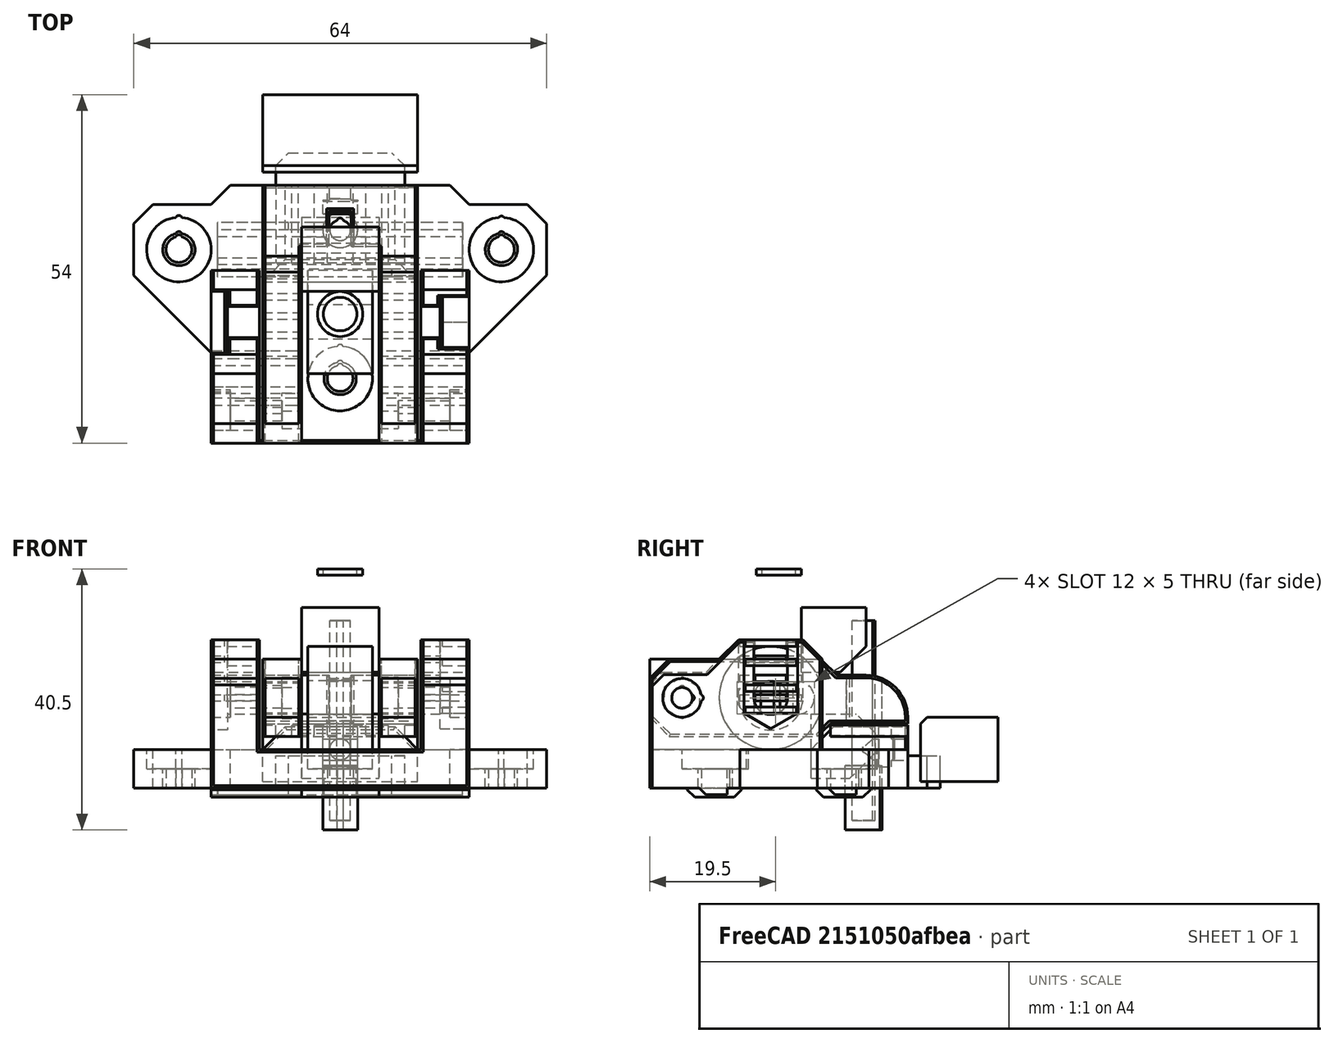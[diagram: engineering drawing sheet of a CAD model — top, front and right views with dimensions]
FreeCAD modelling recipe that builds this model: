
FCSTD DOCUMENT  (FreeCAD 0.18R14555 (Git shallow))
Label: y-idler-10mm-lower-rev
License: All rights reserved
LicenseURL: http://en.wikipedia.org/wiki/All_rights_reserved
objects: Part::Box×72, Part::Cylinder×41, Part::MultiFuse×41, Part::Cut×37, Part::Chamfer×27, Part::Feature×24, Part::Fillet×1
note: 243 computed .brp shape members not serialized (recipe doc carries the construction recipe); baked Part::Feature solids carry a one-line shape summary decoded from their .brp

FEATURE [Part::Box] Box  label="Cube"
  AttacherType = Attacher::AttachEngine3D
  Height = 10
  Length = 40
  Placement = pos=(-20,-20,-10) rot=(0,0,1;0rad)
  Width = 40
FEATURE [Part::Box] Box001  label="Cube001"
  AttacherType = Attacher::AttachEngine3D
  Height = 12
  Length = 6
  Placement = pos=(6,-20,4) rot=(0,0,1;0rad)
  Width = 43
FEATURE [Part::Box] Box002  label="Cube002"
  AttacherType = Attacher::AttachEngine3D
  Height = 12
  Length = 6
  Placement = pos=(-12,-20,4) rot=(0,0,1;0rad)
  Width = 43
FEATURE [Part::Box] Box003  label="Cube003"
  AttacherType = Attacher::AttachEngine3D
  Height = 12
  Length = 12
  Placement = pos=(-6,10.5,3) rot=(0,0,1;0rad)
  Width = 12.5
FEATURE [Part::Cylinder] Cylinder  label="idler"
  Angle = 360
  AttacherType = Attacher::AttachEngine3D
  Height = 10
  Placement = pos=(5,-1.25,10) rot=(0,-1,0;1.5708rad)
  Radius = 8
FEATURE [Part::Cylinder] Cylinder001
  Angle = 360
  AttacherType = Attacher::AttachEngine3D
  Height = 6
  Placement = pos=(6,-2,15) rot=(0,1,0;1.5708rad)
  Radius = 2.5
FEATURE [Part::Cylinder] Cylinder002
  Angle = 360
  AttacherType = Attacher::AttachEngine3D
  Height = 6
  Placement = pos=(-12,5,15) rot=(0,1,0;1.5708rad)
  Radius = 2.5
FEATURE [Part::Cylinder] Cylinder003
  Angle = 360
  AttacherType = Attacher::AttachEngine3D
  Height = 6
  Placement = pos=(-12,-2,15) rot=(0,1,0;1.5708rad)
  Radius = 2.5
FEATURE [Part::Cylinder] Cylinder004
  Angle = 360
  AttacherType = Attacher::AttachEngine3D
  Height = 6
  Placement = pos=(6,5,15) rot=(0,1,0;1.5708rad)
  Radius = 2.5
FEATURE [Part::Box] Box005  label="Cube005"
  AttacherType = Attacher::AttachEngine3D
  Height = 5
  Length = 6
  Placement = pos=(6,-2,12.5) rot=(0,0,1;0rad)
  Width = 7
FEATURE [Part::Box] Box006  label="Cube006"
  AttacherType = Attacher::AttachEngine3D
  Height = 5
  Length = 6
  Placement = pos=(-12,-2,12.5) rot=(0,0,1;0rad)
  Width = 7
FEATURE [Part::MultiFuse] Fusion
  Placement = pos=(0,-2,-5) rot=(0,0,1;0rad)
  Shapes = -> [Box005,Cylinder001,Cylinder004]
FEATURE [Part::MultiFuse] Fusion001
  Placement = pos=(0,-2,-5) rot=(0,0,1;0rad)
  Shapes = -> [Box006,Cylinder003,Cylinder002]
FEATURE [Part::Box] Box007  label="Cube007"
  AttacherType = Attacher::AttachEngine3D
  Height = 14
  Length = 7.5
  Placement = pos=(-20,-20,1) rot=(0,0,1;0rad)
  Width = 11
FEATURE [Part::Box] Box008  label="Cube008"
  AttacherType = Attacher::AttachEngine3D
  Height = 14
  Length = 7.5
  Placement = pos=(12.5,-20,1) rot=(0,0,1;0rad)
  Width = 11
FEATURE [Part::Box] Box009  label="Cube009"
  AttacherType = Attacher::AttachEngine3D
  Height = 20
  Length = 7.5
  Placement = pos=(-20,-10,0) rot=(0,0,1;0rad)
  Width = 18
FEATURE [Part::Box] Box010  label="Cube010"
  AttacherType = Attacher::AttachEngine3D
  Height = 20
  Length = 7.5
  Placement = pos=(12.5,-10,0) rot=(0,0,1;0rad)
  Width = 18
FEATURE [Part::Chamfer] Chamfer
  Base = -> Box009
  Edges = 2 edges r=4: [Edge10,Edge12]
FEATURE [Part::Chamfer] Chamfer001
  Base = -> Box010
  Edges = 2 edges r=4: [Edge10,Edge12]
FEATURE [Part::Cylinder] Cylinder005  label="Cylinder"
  Angle = 360
  AttacherType = Attacher::AttachEngine3D
  Height = 8
  Placement = pos=(-12,0,10) rot=(0,-1,0;1.5708rad)
  Radius = 2.6
FEATURE [Part::Cylinder] Cylinder006  label="Cylinder005"
  Angle = 360
  AttacherType = Attacher::AttachEngine3D
  Height = 8
  Placement = pos=(20,0,10) rot=(0,-1,0;1.5708rad)
  Radius = 2.6
FEATURE [Part::Box] Box011  label="Cube011"
  AttacherType = Attacher::AttachEngine3D
  Height = 10
  Length = 8
  Placement = pos=(12,-2.6,10) rot=(0,0,1;0rad)
  Width = 5.2
FEATURE [Part::Box] Box012  label="Cube012"
  AttacherType = Attacher::AttachEngine3D
  Height = 10
  Length = 8
  Placement = pos=(-20,-2.6,10) rot=(0,0,1;0rad)
  Width = 5.2
FEATURE [Part::Cylinder] Cylinder007  label="Cylinder006"
  Angle = 360
  AttacherType = Attacher::AttachEngine3D
  Height = 31
  Placement = pos=(0,16,-10) rot=(0,0,1;0rad)
  Radius = 1.6
FEATURE [Part::Cylinder] Cylinder008  label="Cylinder007"
  Angle = 360
  AttacherType = Attacher::AttachEngine3D
  Height = 3
  Placement = pos=(25,10,-3) rot=(0,0,1;0rad)
  Radius = 5
FEATURE [Part::Cylinder] Cylinder009  label="Cylinder008"
  Angle = 360
  AttacherType = Attacher::AttachEngine3D
  Height = 8
  Placement = pos=(-12,-15,10) rot=(0,-1,0;1.5708rad)
  Radius = 1.6
FEATURE [Part::Cylinder] Cylinder010  label="Cylinder009"
  Angle = 360
  AttacherType = Attacher::AttachEngine3D
  Height = 8
  Placement = pos=(20,-15,10) rot=(0,-1,0;1.5708rad)
  Radius = 1.6
FEATURE [Part::Cylinder] Cylinder011  label="Cylinder010"
  Angle = 360
  AttacherType = Attacher::AttachEngine3D
  Height = 24
  Placement = pos=(12,-15,10) rot=(0,-1,0;1.5708rad)
  Radius = 1.6
FEATURE [Part::Cylinder] Cylinder012  label="Cylinder011"
  Angle = 360
  AttacherType = Attacher::AttachEngine3D
  Height = 3
  Placement = pos=(-25,10,-3) rot=(0,0,1;0rad)
  Radius = 5
FEATURE [Part::Box] Box014  label="Cube014"
  AttacherType = Attacher::AttachEngine3D
  Height = 10
  Length = 64
  Placement = pos=(-32,-6,-10) rot=(0,0,1;0rad)
  Width = 23
FEATURE [Part::Chamfer] Chamfer004
  Base = -> Box014
  Edges = 2 edges r=12: [Edge1,Edge5]
FEATURE [Part::Chamfer] Chamfer005
  Base = -> Box
  Edges = 2 edges r=3: [Edge3,Edge7]
FEATURE [Part::Chamfer] Chamfer006
  Base = -> Chamfer004
  Edges = 2 edges r=3: [Edge3,Edge13]
FEATURE [Part::Cylinder] Cylinder013  label="Cylinder012"
  Angle = 360
  AttacherType = Attacher::AttachEngine3D
  Height = 24
  Placement = pos=(12,-15,11.4) rot=(0,-1,0;1.5708rad)
  Radius = 0.5
FEATURE [Part::Cylinder] Cylinder014  label="Cylinder013"
  Angle = 360
  AttacherType = Attacher::AttachEngine3D
  Height = 8
  Placement = pos=(20,-13.6,10) rot=(0,-1,0;1.5708rad)
  Radius = 0.5
FEATURE [Part::Cylinder] Cylinder015  label="Cylinder014"
  Angle = 360
  AttacherType = Attacher::AttachEngine3D
  Height = 8
  Placement = pos=(-12,-13.6,10) rot=(0,-1,0;1.5708rad)
  Radius = 0.5
FEATURE [Part::Cylinder] Cylinder016  label="Cylinder015"
  Angle = 360
  AttacherType = Attacher::AttachEngine3D
  Height = 15
  Placement = pos=(-25,10,-10) rot=(0,0,1;0rad)
  Radius = 2.5
FEATURE [Part::Cylinder] Cylinder017  label="Cylinder016"
  Angle = 360
  AttacherType = Attacher::AttachEngine3D
  Height = 15
  Placement = pos=(25,10,-10) rot=(0,0,1;0rad)
  Radius = 2.5
FEATURE [Part::Cylinder] Cylinder018  label="Cylinder019"
  Angle = 360
  AttacherType = Attacher::AttachEngine3D
  Height = 15
  Placement = pos=(25,12.3,-10) rot=(0,0,1;0rad)
  Radius = 0.5
FEATURE [Part::Cylinder] Cylinder019  label="Cylinder020"
  Angle = 360
  AttacherType = Attacher::AttachEngine3D
  Height = 15
  Placement = pos=(-25,12.3,-10) rot=(0,0,1;0rad)
  Radius = 0.5
FEATURE [Part::Cylinder] Cylinder020  label="Cylinder021"
  Angle = 360
  AttacherType = Attacher::AttachEngine3D
  Height = 31
  Placement = pos=(0,17.4,-10) rot=(0,0,1;0rad)
  Radius = 0.5
FEATURE [Part::Cylinder] Cylinder021  label="Cylinder022"
  Angle = 360
  AttacherType = Attacher::AttachEngine3D
  Height = 15
  Placement = pos=(0,-10,-10) rot=(0,0,1;0rad)
  Radius = 2.5
FEATURE [Part::Cylinder] Cylinder023  label="Cylinder024"
  Angle = 360
  AttacherType = Attacher::AttachEngine3D
  Height = 15
  Placement = pos=(0,-7.7,-10) rot=(0,0,1;0rad)
  Radius = 0.5
FEATURE [Part::Cylinder] Cylinder024  label="Cylinder025"
  Angle = 360
  AttacherType = Attacher::AttachEngine3D
  Height = 2.5
  Placement = pos=(-17.5,0,10) rot=(0,-1,0;1.5708rad)
  Radius = 5
FEATURE [Part::Box] Box015  label="Cube015"
  AttacherType = Attacher::AttachEngine3D
  Height = 10
  Length = 2.5
  Placement = pos=(-20,-5,10) rot=(0,0,1;0rad)
  Width = 10
FEATURE [Part::Feature] Fusion010001  label="Fusion011"
  Placement = pos=(0,5.775,5) rot=(0,0,1;0rad)
  shape: bbox 40 x 8.45 x 1.4 mm, 38 faces (baked)
FEATURE [Part::Feature] Fusion010002  label="Fusion012"
  Placement = pos=(12,25.77,5) rot=(0,0,1;0rad)
  shape: bbox 40 x 8.45 x 1.4 mm, 38 faces (baked)
FEATURE [Part::Feature] Fusion010003  label="Fusion013"
  Placement = pos=(-12,25.765,5) rot=(0,0,1;0rad)
  shape: bbox 40 x 8.45 x 1.4 mm, 38 faces (baked)
FEATURE [Part::Cylinder] Cylinder025  label="Cylinder026"
  Angle = 360
  AttacherType = Attacher::AttachEngine3D
  Height = 3
  Placement = pos=(0,-10,-3) rot=(0,0,1;0rad)
  Radius = 5
FEATURE [Part::Cylinder] Cylinder026  label="Cylinder027"
  Angle = 360
  AttacherType = Attacher::AttachEngine3D
  Height = 3
  Placement = pos=(0,-5.2,-3) rot=(0,0,1;0rad)
  Radius = 0.5
FEATURE [Part::Cylinder] Cylinder027  label="Cylinder028"
  Angle = 360
  AttacherType = Attacher::AttachEngine3D
  Height = 3
  Placement = pos=(-25,14.8,-3) rot=(0,0,1;0rad)
  Radius = 0.5
FEATURE [Part::Cylinder] Cylinder028  label="Cylinder029"
  Angle = 360
  AttacherType = Attacher::AttachEngine3D
  Height = 3
  Placement = pos=(25,14.7,-3) rot=(0,0,1;0rad)
  Radius = 0.5
FEATURE [Part::MultiFuse] Fusion010005
  Shapes = -> [Cylinder025,Cylinder012,Cylinder008]
FEATURE [Part::Box] Box017  label="Cube017"
  AttacherType = Attacher::AttachEngine3D
  Height = 10
  Length = 10
  Placement = pos=(-60,0,-20) rot=(0,0,1;0rad)
  Width = 10
FEATURE [Part::Box] Box018  label="Cube018"
  AttacherType = Attacher::AttachEngine3D
  Height = 10
  Length = 10
  Placement = pos=(-40,0,-20) rot=(0,0,1;0rad)
  Width = 10
FEATURE [Part::Box] Box019  label="Cube019"
  AttacherType = Attacher::AttachEngine3D
  Height = 10
  Length = 10
  Placement = pos=(40,0,-20) rot=(0,0,1;0rad)
  Width = 10
FEATURE [Part::Box] Box020  label="Cube020"
  AttacherType = Attacher::AttachEngine3D
  Height = 10
  Length = 10
  Placement = pos=(40,0,-20) rot=(0,0,1;0rad)
  Width = 10
FEATURE [Part::Chamfer] Chamfer016
  Base = -> Box018
  Edges = 1 edges r=4: [Edge5]
  Placement = pos=(0,12,5) rot=(0,0,1;0rad)
FEATURE [Part::Chamfer] Chamfer017
  Base = -> Box017
  Edges = 1 edges r=4: [Edge7]
  Placement = pos=(20,-2,5) rot=(0,0,1;0rad)
FEATURE [Part::Chamfer] Chamfer018
  Base = -> Box019
  Edges = 1 edges r=4: [Edge3]
  Placement = pos=(-11,-3,5) rot=(0,0,1;0rad)
FEATURE [Part::Chamfer] Chamfer019
  Base = -> Box020
  Edges = 1 edges r=4: [Edge1]
  Placement = pos=(-9,11,5) rot=(0,0,1;0rad)
FEATURE [Part::Cylinder] Cylinder030  label="Cylinder031"
  Angle = 360
  AttacherType = Attacher::AttachEngine3D
  Height = 3
  Placement = pos=(-20,-12.2,10) rot=(0,1,0;1.5708rad)
  Radius = 0.5
FEATURE [Part::Cylinder] Cylinder031  label="Cylinder032"
  Angle = 360
  AttacherType = Attacher::AttachEngine3D
  Height = 3
  Placement = pos=(-20,-15,10) rot=(0,1,0;1.5708rad)
  Radius = 3
FEATURE [Part::Feature] Body005001  label="Body006"
  Placement = pos=(-9,-15,10) rot=(1,0,0;1.5708rad)
  shape: bbox 3 x 5.543 x 6.4 mm, 8 faces (baked)
FEATURE [Part::Cylinder] Cylinder032  label="Cylinder033"
  Angle = 360
  AttacherType = Attacher::AttachEngine3D
  Height = 3
  Placement = pos=(17,-15,10) rot=(0,1,0;1.5708rad)
  Radius = 3
FEATURE [Part::Cylinder] Cylinder033  label="Cylinder034"
  Angle = 360
  AttacherType = Attacher::AttachEngine3D
  Height = 3
  Placement = pos=(17,-12.2,10) rot=(0,1,0;1.5708rad)
  Radius = 0.5
FEATURE [Part::MultiFuse] Fusion010006003
  Shapes = -> [Cylinder031,Cylinder030]
FEATURE [Part::MultiFuse] Fusion010006004
  Shapes = -> [Cylinder033,Cylinder032]
FEATURE [Part::Feature] Body005002  label="Body007"
  Placement = pos=(6,-15,10) rot=(1,0,0;1.5708rad)
  shape: bbox 3 x 5.543 x 6.4 mm, 8 faces (baked)
FEATURE [Part::Box] Box029  label="Cube029"
  AttacherType = Attacher::AttachEngine3D
  Height = 1
  Length = 2.1
  Placement = pos=(-20,-3.53,7.5) rot=(0,0,1;0rad)
  Width = 9.6
FEATURE [Part::Box] Box030  label="Cube030"
  AttacherType = Attacher::AttachEngine3D
  Height = 1
  Length = 4.1
  Placement = pos=(15.9,-2.68,5.6) rot=(0,0,1;0rad)
  Width = 7.91
FEATURE [Part::Box] Box032  label="Cube032"
  AttacherType = Attacher::AttachEngine3D
  Height = 1
  Length = 5
  Placement = pos=(-17.5,-1.13,7.5) rot=(0,0,1;0rad)
  Width = 4.8
FEATURE [Part::MultiFuse] Fusion010006008
  Shapes = -> [Box012,Cylinder005]
FEATURE [Part::MultiFuse] Fusion010006009
  Shapes = -> [Cylinder006,Box011]
FEATURE [Part::Cut] Cut022015
  Base = -> Chamfer
  Tool = -> Fusion010006008
FEATURE [Part::Cut] Cut022016
  Base = -> Chamfer001
  Tool = -> Fusion010006009
FEATURE [Part::Feature] Pad002001  label="Pad003"
  Placement = pos=(17.5,0,10) rot=(0.57735,0.57735,0.57735;2.0944rad)
  shape: bbox 10 x 8.314 x 9.6 mm, 8 faces (baked)
FEATURE [Part::Feature] Pad002002  label="Pad004"
  Placement = pos=(17.5,0,14) rot=(0.57735,0.57735,0.57735;2.0944rad)
  shape: bbox 10 x 8.314 x 9.6 mm, 8 faces (baked)
FEATURE [Part::Feature] Pad002003  label="Pad005"
  Placement = pos=(17.5,0,18) rot=(0.57735,0.57735,0.57735;2.0944rad)
  shape: bbox 10 x 8.314 x 9.6 mm, 8 faces (baked)
FEATURE [Part::MultiFuse] Fusion010006010
  Shapes = -> [Pad002003,Pad002001,Pad002002]
FEATURE [Part::Cut] Cut022017  label="base-right-arm-top"
  Base = -> Cut022016
  Placement = pos=(0,1.27,-2) rot=(0,0,1;0rad)
  Tool = -> Fusion010006010
FEATURE [Part::MultiFuse] Fusion010006011
  Shapes = -> [Cylinder024,Box015]
FEATURE [Part::Cut] Cut022018  label="base-left-arm-top"
  Base = -> Cut022015
  Placement = pos=(0,1.27,-2) rot=(0,0,1;0rad)
  Tool = -> Fusion010006011
FEATURE [Part::MultiFuse] Fusion010006014
  Shapes = -> [Cylinder013,Cylinder011]
FEATURE [Part::MultiFuse] Fusion010006015
  Placement = pos=(0,0,-1) rot=(0,0,1;0rad)
  Shapes = -> [Fusion010006014,Body005002,Body005001]
FEATURE [Part::MultiFuse] Fusion010006012003
  Placement = pos=(0,0,-1) rot=(0,0,1;0rad)
  Shapes = -> [Fusion010006003,Cylinder015,Cylinder009]
FEATURE [Part::MultiFuse] Fusion010006012004
  Placement = pos=(0,0,-1) rot=(0,0,1;0rad)
  Shapes = -> [Cylinder010,Cylinder014,Fusion010006004]
FEATURE [Part::MultiFuse] Fusion010006012005
  Placement = pos=(0,0,5) rot=(0,0,1;0rad)
  Shapes = -> [Chamfer006,Chamfer005]
FEATURE [Part::Box] Box038  label="Cube038"
  AttacherType = Attacher::AttachEngine3D
  Height = 5
  Length = 65
  Placement = pos=(-32,-24,1) rot=(0,0,1;0rad)
  Width = 50
FEATURE [Part::MultiFuse] Fusion010006012007
  Shapes = -> [Chamfer018,Chamfer019,Chamfer016,Chamfer017]
FEATURE [Part::MultiFuse] Fusion010006012008
  Placement = pos=(0,0,1) rot=(0,0,1;0rad)
  Shapes = -> [Fusion010005,Cylinder027,Cylinder028,Cylinder026]
FEATURE [Part::Box] Box039  label="Cube039"
  AttacherType = Attacher::AttachEngine3D
  Height = 10
  Length = 40
  Placement = pos=(-26,-25,12) rot=(0,0,1;0rad)
  Width = 20
FEATURE [Part::Chamfer] Chamfer027
  Base = -> Box039
  Edges = 1 edges r=2: [Edge11]
  Placement = pos=(0,-4.25,1) rot=(0,0,1;0rad)
FEATURE [Part::Box] Box040  label="Cube040"
  AttacherType = Attacher::AttachEngine3D
  Height = 10
  Length = 32
  Placement = pos=(-15,24,-8) rot=(0,0,1;0rad)
  Width = 26
FEATURE [Part::Chamfer] Chamfer028
  Base = -> Box040
  Edges = 1 edges r=3: [Edge10]
  Placement = pos=(0,-19,3) rot=(0,0,1;0rad)
FEATURE [Part::Box] Box043  label="cube042"
  AttacherType = Attacher::AttachEngine3D
  Height = 2.8
  Length = 2
  Placement = pos=(-12,11,2) rot=(0,0,1;0rad)
  Width = 12
FEATURE [Part::Box] Box044  label="Cube043"
  AttacherType = Attacher::AttachEngine3D
  Height = 4.6
  Length = 6
  Placement = pos=(-12,-2,5.7) rot=(0,0,1;0rad)
  Width = 1
FEATURE [Part::Box] Box045  label="Cube044"
  AttacherType = Attacher::AttachEngine3D
  Height = 4.6
  Length = 6
  Placement = pos=(6,-2,5.7) rot=(0,0,1;0rad)
  Width = 1
FEATURE [Part::Box] Box052  label="Cube047"
  AttacherType = Attacher::AttachEngine3D
  Height = 4.6
  Length = 6
  Placement = pos=(-12,1,5.7) rot=(0,0,1;0rad)
  Width = 1
FEATURE [Part::Box] Box054  label="Cube049"
  AttacherType = Attacher::AttachEngine3D
  Height = 4.6
  Length = 6
  Placement = pos=(-12,4,5.7) rot=(0,0,1;0rad)
  Width = 1
FEATURE [Part::Box] Box055  label="Cube050"
  AttacherType = Attacher::AttachEngine3D
  Height = 4.6
  Length = 6
  Placement = pos=(6,1,5.7) rot=(0,0,1;0rad)
  Width = 1
FEATURE [Part::Box] Box057  label="Cube052"
  AttacherType = Attacher::AttachEngine3D
  Height = 4.6
  Length = 6
  Placement = pos=(6,4,5.7) rot=(0,0,1;0rad)
  Width = 1
FEATURE [Part::Box] Box058  label="Cube053"
  AttacherType = Attacher::AttachEngine3D
  Height = 1
  Length = 4.1
  Placement = pos=(15.9,-2.68,9) rot=(0,0,1;0rad)
  Width = 7.91
FEATURE [Part::Box] Box059  label="Cube054"
  AttacherType = Attacher::AttachEngine3D
  Height = 1
  Length = 3
  Placement = pos=(12.5,-1.13,7.5) rot=(0,0,1;0rad)
  Width = 4.8
FEATURE [Part::Box] Box063  label="Cube058"
  AttacherType = Attacher::AttachEngine3D
  Height = 1
  Length = 3
  Placement = pos=(12.5,-1.13,10.5) rot=(0,0,1;0rad)
  Width = 4.8
FEATURE [Part::Box] Box064  label="Cube059"
  AttacherType = Attacher::AttachEngine3D
  Height = 1
  Length = 2.1
  Placement = pos=(-20,-3.53,10.5) rot=(0,0,1;0rad)
  Width = 9.6
FEATURE [Part::Box] Box066  label="Cube061"
  AttacherType = Attacher::AttachEngine3D
  Height = 1
  Length = 5
  Placement = pos=(-17.5,-1.13,10.5) rot=(0,0,1;0rad)
  Width = 4.8
FEATURE [Part::Box] Box068  label="Cube063"
  AttacherType = Attacher::AttachEngine3D
  Height = 1
  Length = 3
  Placement = pos=(12.5,-1.13,13.5) rot=(0,0,1;0rad)
  Width = 4.8
FEATURE [Part::Box] Box069  label="Cube064"
  AttacherType = Attacher::AttachEngine3D
  Height = 1
  Length = 2.1
  Placement = pos=(-20,-3.53,13.5) rot=(0,0,1;0rad)
  Width = 9.6
FEATURE [Part::Box] Box070  label="Cube065"
  AttacherType = Attacher::AttachEngine3D
  Height = 1
  Length = 2.1
  Placement = pos=(-20,-3.53,16) rot=(0,0,1;0rad)
  Width = 9.6
FEATURE [Part::Box] Box071  label="Cube066"
  AttacherType = Attacher::AttachEngine3D
  Height = 1
  Length = 5
  Placement = pos=(-17.5,-1.13,16) rot=(0,0,1;0rad)
  Width = 4.8
FEATURE [Part::Box] Box075  label="Cube070"
  AttacherType = Attacher::AttachEngine3D
  Height = 1
  Length = 3
  Placement = pos=(12.5,-1.13,16) rot=(0,0,1;0rad)
  Width = 4.8
FEATURE [Part::Box] Box076  label="Cube071"
  AttacherType = Attacher::AttachEngine3D
  Height = 1
  Length = 5
  Placement = pos=(-17.5,-1.13,13) rot=(0,0,1;0rad)
  Width = 4.8
FEATURE [Part::Box] Box077  label="Cube072"
  AttacherType = Attacher::AttachEngine3D
  Height = 1
  Length = 4.1
  Placement = pos=(15.9,-2.68,16) rot=(0,0,1;0rad)
  Width = 7.91
FEATURE [Part::Box] Box078  label="Cube073"
  AttacherType = Attacher::AttachEngine3D
  Height = 1
  Length = 4.1
  Placement = pos=(15.9,-2.68,13) rot=(0,0,1;0rad)
  Width = 7.91
FEATURE [Part::Box] Box079  label="Cube074"
  AttacherType = Attacher::AttachEngine3D
  Height = 17
  Length = 10
  Placement = pos=(-21,-15,0) rot=(0,0,1;0rad)
  Width = 14
FEATURE [Part::Chamfer] Chamfer030006
  Base = -> Box079
  Edges = 1 edges r=10: [Edge11]
  Placement = pos=(0,2.27,12) rot=(0,0,1;0rad)
FEATURE [Part::Feature] Chamfer030006001  label="Chamfer030007"
  Placement = pos=(32,2.27,12) rot=(0,0,1;0rad)
  shape: bbox 10 x 14 x 17 mm, 7 faces (baked)
FEATURE [Part::Cut] Cut022020016004
  Base = -> Cut022018
  Tool = -> Chamfer030006
FEATURE [Part::Cut] Cut022020016005
  Base = -> Cut022017
  Tool = -> Chamfer030006001
FEATURE [Part::Box] Box080  label="Cube075"
  AttacherType = Attacher::AttachEngine3D
  Height = 10
  Length = 12
  Placement = pos=(-21,-5,17) rot=(0,0,1;0rad)
  Width = 16
FEATURE [Part::Cut] Cut022020016006  label="base-left-arm-top-trim"
  Base = -> Cut022020016004
  Placement = pos=(0,-2.52,1) rot=(0,0,1;0rad)
  Tool = -> Box080
FEATURE [Part::Box] Box081  label="Cube076"
  AttacherType = Attacher::AttachEngine3D
  Height = 10
  Length = 12
  Placement = pos=(9,-5,17) rot=(0,0,1;0rad)
  Width = 16
FEATURE [Part::Cut] Cut022020016007  label="base-right-arm-top-trim"
  Base = -> Cut022020016005
  Placement = pos=(0,2.54,0) rot=(0,0,1;0rad)
  Tool = -> Box081
FEATURE [Part::MultiFuse] Fusion010006012010005014
  Shapes = -> [Box071,Box076,Box066,Box032]
FEATURE [Part::MultiFuse] Fusion010006012010005016
  Shapes = -> [Box029,Box064,Box069,Box070]
FEATURE [Part::Box] Box082  label="Cube077"
  AttacherType = Attacher::AttachEngine3D
  Height = 14
  Length = 2
  Placement = pos=(17.55,-3.1,3) rot=(0,0,1;0rad)
  Width = 9
FEATURE [Part::Feature] Chamfer030006002001  label="arm-rev-4-3-no-support001"
  shape: bbox 64 x 40 x 23.4 mm, 138 faces (baked)
FEATURE [Part::Cut] Cut022020016008
  Base = -> Box082
  Placement = pos=(-2.05,2.54,0) rot=(0,0,1;0rad)
  Tool = -> Chamfer030006002001
FEATURE [Part::MultiFuse] Fusion010006012010005012002
  Shapes = -> [Box059,Box075,Box063,Box068]
FEATURE [Part::MultiFuse] Fusion010006012010005012003
  Shapes = -> [Box030,Box078,Box058,Box077]
FEATURE [Part::MultiFuse] Fusion010006012010005012004  label="base-custom-support"
  Placement = pos=(0,-2.52,1) rot=(0,0,1;0rad)
  Shapes = -> [Fusion010006012010005016,Fusion010006012010005012002,Fusion010006012010005012003,Fusion010006012010005014]
FEATURE [Part::Box] Box083  label="Cube078"
  AttacherType = Attacher::AttachEngine3D
  Height = 10
  Length = 12
  Placement = pos=(-6,-15,-15) rot=(0,0,1;0rad)
  Width = 10
FEATURE [Part::Box] Box084  label="Cube079"
  AttacherType = Attacher::AttachEngine3D
  Height = 10
  Length = 13
  Placement = pos=(19,5,-15) rot=(0,0,1;0rad)
  Width = 10
FEATURE [Part::Box] Box085  label="Cube080"
  AttacherType = Attacher::AttachEngine3D
  Height = 10
  Length = 13
  Placement = pos=(-32,5,-15) rot=(0,0,1;0rad)
  Width = 10
FEATURE [Part::Cut] Cut022020016019  label="base-right-arm-top-cut"
  Base = -> Cut022020016007
  Placement = pos=(0,-5.06,1) rot=(0,0,1;0rad)
  Tool = -> Cut022020016008
FEATURE [Part::Cylinder] Cylinder038  label="Cylinder039"
  Angle = 360
  AttacherType = Attacher::AttachEngine3D
  Height = 10
  Placement = pos=(0,13,-11.5) rot=(0,0,1;0rad)
  Radius = 2.7
FEATURE [Part::Cylinder] Cylinder039  label="Cylinder040"
  Angle = 360
  AttacherType = Attacher::AttachEngine3D
  Height = 10
  Placement = pos=(0,15.5,-11.5) rot=(0,0,1;0rad)
  Radius = 0.5
FEATURE [Part::Box] Box087  label="cube043"
  AttacherType = Attacher::AttachEngine3D
  Height = 2.8
  Length = 1
  Placement = pos=(-7.5,11,2) rot=(0,0,1;0rad)
  Width = 12
FEATURE [Part::Box] Box089  label="cube045"
  AttacherType = Attacher::AttachEngine3D
  Height = 2.8
  Length = 2
  Placement = pos=(-4,11,2) rot=(0,0,1;0rad)
  Width = 12
FEATURE [Part::Box] Box090  label="cube046"
  AttacherType = Attacher::AttachEngine3D
  Height = 2.8
  Length = 2
  Placement = pos=(10,11,2) rot=(0,0,1;0rad)
  Width = 12
FEATURE [Part::Box] Box091  label="cube047"
  AttacherType = Attacher::AttachEngine3D
  Height = 2.8
  Length = 1
  Placement = pos=(6.5,11,2) rot=(0,0,1;0rad)
  Width = 12
FEATURE [Part::Box] Box093  label="cube049"
  AttacherType = Attacher::AttachEngine3D
  Height = 2.8
  Length = 2
  Placement = pos=(2,11,2) rot=(0,0,1;0rad)
  Width = 12
FEATURE [Part::Box] Box095  label="Cube083"
  AttacherType = Attacher::AttachEngine3D
  Height = 5
  Length = 20
  Placement = pos=(-10,20,-5) rot=(0,0,1;0rad)
  Width = 5
FEATURE [Part::Chamfer] Chamfer030006002012
  Base = -> Box095
  Edges = 2 edges r=2: [Edge3,Edge7]
FEATURE [Part::MultiFuse] Fusion010006012010005012005015
  Placement = pos=(0,1.5,1) rot=(0,0,1;0rad)
  Shapes = -> [Box090,Box091,Box093,Box089,Box087,Box043]
FEATURE [Part::MultiFuse] Fusion010006012010005012005016
  Placement = pos=(0,-1.79,1) rot=(0,0,1;0rad)
  Shapes = -> [Box045,Box055,Box057]
FEATURE [Part::MultiFuse] Fusion010006012010005012005017
  Placement = pos=(0,-1.79,1) rot=(0,0,1;0rad)
  Shapes = -> [Box052,Box054,Box044]
FEATURE [Part::Box] Box096  label="Cube084"
  AttacherType = Attacher::AttachEngine3D
  Height = 10
  Length = 12
  Placement = pos=(-6,0,12) rot=(0,0,1;0rad)
  Width = 10
FEATURE [Part::Chamfer] Chamfer030006002016
  Base = -> Box096
  Edges = 1 edges r=4: [Edge11]
  Placement = pos=(0,3.5,1) rot=(0,0,1;0rad)
FEATURE [Part::Cylinder] Cylinder040  label="Cylinder041"
  Angle = 360
  AttacherType = Attacher::AttachEngine3D
  Height = 5
  Placement = pos=(0,16,-5) rot=(0,0,1;0rad)
  Radius = 3.1
FEATURE [Part::Box] Box098  label="Cube086"
  AttacherType = Attacher::AttachEngine3D
  Height = 7
  Length = 5.4
  Placement = pos=(-2.7,18.5,-1.7) rot=(0,0,1;0rad)
  Width = 2.4
FEATURE [Part::Cylinder] Cylinder041  label="Cylinder042"
  Angle = 360
  AttacherType = Attacher::AttachEngine3D
  Height = 27
  Placement = pos=(0,16,-9) rot=(0,0,1;0rad)
  Radius = 1.6
FEATURE [Part::Cylinder] Cylinder042  label="Cylinder043"
  Angle = 360
  AttacherType = Attacher::AttachEngine3D
  Height = 27
  Placement = pos=(0,17.4,-9) rot=(0,0,1;0rad)
  Radius = 0.5
FEATURE [Part::MultiFuse] Fusion010006012010005012005020  label="screw-hole-cut"
  Placement = pos=(0,-3,0) rot=(0,0,1;0rad)
  Shapes = -> [Cylinder040,Cylinder042,Cylinder041]
FEATURE [Part::Cylinder] Cylinder043  label="Cylinder044"
  Angle = 360
  AttacherType = Attacher::AttachEngine3D
  Height = 18
  Placement = pos=(0,16,1) rot=(-1,0,0;1.5708rad)
  Radius = 1.65
FEATURE [Part::Box] Box099  label="Cube087"
  AttacherType = Attacher::AttachEngine3D
  Height = 6.5
  Length = 1.35
  Placement = pos=(-3,20.7,-2) rot=(0,0,1;0rad)
  Width = 0.2
FEATURE [Part::Box] Box100  label="Cube088"
  AttacherType = Attacher::AttachEngine3D
  Height = 6.5
  Length = 1.35
  Placement = pos=(1.65,20.7,-2) rot=(0,0,1;0rad)
  Width = 0.2
FEATURE [Part::Box] Box101  label="Cube089"
  AttacherType = Attacher::AttachEngine3D
  Height = 1.35
  Length = 6
  Placement = pos=(-3,20.5,-2) rot=(0,0,1;0rad)
  Width = 0.4
FEATURE [Part::Box] Box102  label="Cube090"
  AttacherType = Attacher::AttachEngine3D
  Height = 1.85
  Length = 6
  Placement = pos=(-3,20.5,2.65) rot=(0,0,1;0rad)
  Width = 0.4
FEATURE [Part::MultiFuse] Fusion010006012010005012005024
  Shapes = -> [Box101,Box099,Box100,Box102]
FEATURE [Part::Cut] Cut022020016032007004
  Base = -> Box098
  Tool = -> Fusion010006012010005012005024
FEATURE [Part::MultiFuse] Fusion010006012010005012005025  label="grub-screw-hole-cut"
  Placement = pos=(0,-3,0) rot=(0,0,1;0rad)
  Shapes = -> [Cut022020016032007004,Cylinder043]
FEATURE [Part::Box] Box103  label="Cube091"
  AttacherType = Attacher::AttachEngine3D
  Height = 30
  Length = 3.4
  Placement = pos=(-1.7,9,0) rot=(0,0,1;0rad)
  Width = 7
FEATURE [Part::Feature] Chamfer030006002016001  label="Chamfer030006002025"
  Placement = pos=(0,5.5,-22.5) rot=(0,0,1;0rad)
  shape: bbox 12 x 10 x 10 mm, 7 faces (baked)
FEATURE [Part::Chamfer] Chamfer030006002016002
  Base = -> Chamfer030006002016001
  Edges = 1 edges r=3: [Edge8]
  Placement = pos=(0,-0.5,7) rot=(0,0,1;0rad)
FEATURE [Part::Box] Box105  label="Cube093"
  AttacherType = Attacher::AttachEngine3D
  Height = 10
  Length = 24
  Placement = pos=(-12,17,0) rot=(0,0,1;0rad)
  Width = 12
FEATURE [Part::Chamfer] Chamfer030006002016005006
  Base = -> Box105
  Edges = 1 edges r=1: [Edge10]
  Placement = pos=(0,5,-4) rot=(0,0,1;0rad)
FEATURE [Part::Cut] Cut022020016032007027
  Base = -> Fusion010006012005
  Tool = -> Box038
FEATURE [Part::Cut] Cut022020016032007028
  Base = -> Cut022020016032007027
  Tool = -> Fusion010006012007
FEATURE [Part::MultiFuse] Fusion010006012010005012005027003
  Shapes = -> [Fusion010003,Fusion010001,Fusion010002,Cut022020016032007028]
FEATURE [Part::Cut] Cut022020016032007029
  Base = -> Fusion010006012010005012005027003
  Tool = -> Box085
FEATURE [Part::Cut] Cut022020016032007030
  Base = -> Cut022020016032007029
  Tool = -> Box083
FEATURE [Part::Cut] Cut022020016032007031
  Base = -> Cut022020016032007030
  Tool = -> Box084
FEATURE [Part::Cut] Cut
  Base = -> Box002
  Placement = pos=(0,0,-1) rot=(0,0,1;0rad)
  Tool = -> Fusion001
FEATURE [Part::Cut] Cut022020016032007036002
  Base = -> Box001
  Placement = pos=(0,0,-1) rot=(0,0,1;0rad)
  Tool = -> Fusion
FEATURE [Part::Box] Box106  label="Cube094"
  AttacherType = Attacher::AttachEngine3D
  Height = 10
  Length = 24
  Placement = pos=(-12,10.5,12.5) rot=(0,0,1;0rad)
  Width = 21
FEATURE [Part::Chamfer] Chamfer030006002016005008003006
  Base = -> Box106
  Edges = 1 edges r=3: [Edge9]
  Placement = pos=(0,-4.5,0) rot=(0,0,1;0rad)
FEATURE [Part::MultiFuse] Fusion010006012010005012005027007
  Shapes = -> [Cut,Box003,Cut022020016032007036002]
FEATURE [Part::Cut] Cut022020016032007036009
  Base = -> Fusion010006012010005012005027007
  Tool = -> Fusion010006015
FEATURE [Part::Box] Box107  label="Cube095"
  AttacherType = Attacher::AttachEngine3D
  Height = 10
  Length = 24
  Placement = pos=(-12,12,4.8) rot=(0,0,1;0rad)
  Width = 13
FEATURE [Part::MultiFuse] Fusion010006012010005012005027010
  Shapes = -> [Cylinder021,Cylinder023,Cylinder016,Cylinder019,Cylinder017,Cylinder018]
FEATURE [Part::Cut] Cut022020016032007036015
  Base = -> Cut022020016032007031
  Tool = -> Fusion010006012010005012005027010
FEATURE [Part::Cut] Cut022020016032007036016
  Base = -> Cut022020016032007036015
  Tool = -> Fusion010006012008
FEATURE [Part::MultiFuse] Fusion010006012010005012005027011
  Placement = pos=(0,-3,0) rot=(0,0,1;0rad)
  Shapes = -> [Cylinder007,Cylinder020]
FEATURE [Part::Box] Box108  label="Cube096"
  AttacherType = Attacher::AttachEngine3D
  Height = 9.5
  Length = 24
  Placement = pos=(-12,5,-5) rot=(0,0,1;0rad)
  Width = 15
FEATURE [Part::Chamfer] Chamfer030006002016005008003009003
  Base = -> Box108
  Edges = 3 edges r=3.5: [Edge2,Edge6,Edge10]
FEATURE [Part::Chamfer] Chamfer030006002016005008003009004
  Base = -> Chamfer030006002016005008003009003
  Edges = 3 edges r=0.4: [Edge10,Edge14,Edge15]
FEATURE [Part::MultiFuse] Fusion010006012010005012005027012
  Shapes = -> [Cylinder038,Cylinder039]
FEATURE [Part::Feature] Fusion010006012010005012005027011001  label="Fusion010006012010005012005027013"
  Placement = pos=(0,-3,0) rot=(0,0,1;0rad)
  shape: bbox 3.2 x 3.5 x 31 mm, 9 faces (baked)
FEATURE [Part::Cut] Cut022020016032007036017
  Base = -> Cut022020016032007036016
  Tool = -> Fusion010006012010005012005027011
FEATURE [Part::Feature] Fusion010006012010005012005027012001  label="Fusion010006012010005012005027014"
  shape: bbox 5.4 x 5.7 x 10 mm, 9 faces (baked)
FEATURE [Part::Cut] Cut022020016032007036018
  Base = -> Cut022020016032007036017
  Tool = -> Fusion010006012010005012005027012
FEATURE [Part::Cut] Cut022020016032007036019
  Base = -> Chamfer030006002016005008003009004
  Tool = -> Fusion010006012010005012005020
FEATURE [Part::MultiFuse] Fusion010006012010005012005027012002
  Shapes = -> [Cut022020016032007036018,Cut022020016032007036019]
FEATURE [Part::Cut] Cut022020016032007036020  label="base-plate"
  Base = -> Fusion010006012010005012005027012002
  Tool = -> Fusion010006012010005012005025
FEATURE [Part::Box] Box109  label="Cube097"
  AttacherType = Attacher::AttachEngine3D
  Height = 20
  Length = 26
  Placement = pos=(-13,20,0) rot=(0,0,1;0rad)
  Width = 9
FEATURE [Part::Cut] Cut022020016032007036021
  Base = -> Cut022020016032007036009
  Tool = -> Chamfer027
FEATURE [Part::Cut] Cut022020016032007036022
  Base = -> Cut022020016032007036021
  Tool = -> Box109
FEATURE [Part::Cut] Cut022020016032007036023
  Base = -> Cut022020016032007036022
  Tool = -> Chamfer030006002016005008003006
FEATURE [Part::Fillet] Fillet
  Base = -> Cut022020016032007036023
  Edges = 1 edges r=6.5: [Edge23]
FEATURE [Part::Cut] Cut022020016032007036024
  Base = -> Fillet
  Tool = -> Chamfer028
FEATURE [Part::Cylinder] Cylinder044  label="idler001"
  Angle = 360
  AttacherType = Attacher::AttachEngine3D
  Height = 10
  Placement = pos=(5,-1.25,10) rot=(0,-1,0;1.5708rad)
  Radius = 2.65
FEATURE [Part::Cut] Cut022020016032007036026  label="idler-template"
  Base = -> Cylinder
  Placement = pos=(0,0,-1) rot=(0,0,1;0rad)
  Tool = -> Cylinder044
FEATURE [Part::Cut] Cut022020016032007036027
  Base = -> Fusion010006012010005012005015
  Placement = pos=(0,-4.5,0) rot=(0,0,1;0rad)
  Tool = -> Box107
FEATURE [Part::MultiFuse] Fusion010006012010005012005027012004  label="arm-custom-support"
  Shapes = -> [Cut022020016032007036027,Fusion010006012010005012005017,Fusion010006012010005012005016]
FEATURE [Part::Feature] Fusion010006012010005012005027012006001  label="base-rev-7-basic001"
  shape: bbox 64 x 40 x 24.4 mm, 132 faces (baked)
FEATURE [Part::Chamfer] Chamfer030006002016005008003009008  label="base-rev-7"
  Base = -> Fusion010006012010005012005027012006001
  Edges = 36 edges r=0.4: [Edge2,Edge4,Edge6,Edge8,Edge9,Edge19,Edge21,Edge22,Edge24,Edge25,Edge28,Edge31,Edge41,Edge43,Edge45,Edge46,Edge67,Edge83,Edge84,Edge86,Edge88,Edge89,Edge91,Edge92,Edge94,Edge125,Edge126,Edge146,Edge147,Edge149,Edge151,Edge163,Edge170,Edge171,Edge172,Edge173]
FEATURE [Part::Feature] Part__Feature002  label="m5-to-m4-bolt-hole"
  Placement = pos=(0,-10,-5) rot=(-1,0,0;1.5708rad)
  shape: bbox 6 x 6 x 3 mm, 5 faces (baked)
FEATURE [Part::Feature] Part__Feature003  label="m5-to-m4-bolt-hole001"
  Placement = pos=(25,10,-5) rot=(-1,0,0;1.5708rad)
  shape: bbox 6 x 6 x 3 mm, 5 faces (baked)
FEATURE [Part::Feature] Part__Feature004  label="m5-to-m4-bolt-hole002"
  Placement = pos=(-25,10,-5) rot=(-1,0,0;1.5708rad)
  shape: bbox 6 x 6 x 3 mm, 5 faces (baked)
FEATURE [Part::Feature] Part__Feature  label="tslot-vertical-align"
  Placement = pos=(-30,4.78,-5) rot=(-1,0,0;1.5708rad)
  shape: bbox 60 x 10.45 x 5 mm, 10 faces (baked)
FEATURE [Part::Feature] Part__Feature005  label="tslot-vertical-align001"
  Placement = pos=(-30,-15.22,-5) rot=(-1,0,0;1.5708rad)
  shape: bbox 60 x 10.45 x 5 mm, 10 faces (baked)
FEATURE [Part::Cut] Cut022020016032007036028
  Base = -> Chamfer030006002016005008003009008
  Tool = -> Part__Feature
FEATURE [Part::Cut] Cut022020016032007036029
  Base = -> Cut022020016032007036028
  Tool = -> Part__Feature005
FEATURE [Part::MultiFuse] Fusion010006012010005012005027012006002
  Shapes = -> [Part__Feature003,Cut022020016032007036029,Part__Feature002,Part__Feature004]
FEATURE [Part::Feature] Fusion010006012010005012005027012006002001  label="old"
  shape: bbox 64 x 40 x 24 mm, 155 faces (baked)
FEATURE [Part::Cylinder] Cylinder045
  Angle = 360
  AttacherType = Attacher::AttachEngine3D
  Height = 1
  Radius = 2.6
FEATURE [Part::Cylinder] Cylinder046
  Angle = 360
  AttacherType = Attacher::AttachEngine3D
  Height = 1
  Radius = 3.5
FEATURE [Part::Cut] Cut022020016032007036030  label="washer"
  Base = -> Cylinder046
  Placement = pos=(0,0,28) rot=(0,0,1;0rad)
  Tool = -> Cylinder045
FEATURE [Part::Cut] Cut022020016032007036025
  Base = -> Cut022020016032007036024
  Tool = -> Box103
FEATURE [Part::Box] Box110  label="Cube098"
  AttacherType = Attacher::AttachEngine3D
  Height = 2
  Length = 6
  Placement = pos=(-12,-20,13) rot=(0,0,1;0rad)
  Width = 11
FEATURE [Part::Box] Box111  label="Cube099"
  AttacherType = Attacher::AttachEngine3D
  Height = 2
  Length = 6
  Placement = pos=(6,-20,13) rot=(0,0,1;0rad)
  Width = 11
FEATURE [Part::MultiFuse] Fusion010006012010005012005027012006002003
  Shapes = -> [Cut022020016032007036025,Box110,Box111]
FEATURE [Part::Chamfer] Chamfer030006002016005008003009009
  Base = -> Fusion010006012010005012005027012006002003
  Edges = 2 edges r=3: [Edge30,Edge144]
FEATURE [Part::Feature] Chamfer030006002016005008003009009001  label="Chamfer030006002016005008003009010"
  shape: bbox 24 x 40 x 12 mm, 52 faces (baked)
FEATURE [Part::Chamfer] Chamfer030006002016005008003009009002
  Base = -> Chamfer030006002016005008003009009001
  Edges = 2 edges r=3: [Edge104,Edge106]
FEATURE [Part::Chamfer] Chamfer030006002016005008003009009003  label="arm-rev-7-eainforce"
  Base = -> Chamfer030006002016005008003009009002
  Edges = 53 edges r=0.4: [Edge1,Edge2,Edge3,Edge4,Edge5,Edge6,Edge7,Edge8,Edge9,Edge10,Edge11,Edge19,Edge23,Edge25,Edge27,Edge29,Edge31,Edge33,Edge35,Edge37,Edge38,Edge39,Edge41,Edge42,Edge43,Edge44,Edge45,Edge46,Edge47,Edge48,Edge49,Edge50,Edge52,Edge54,Edge76,Edge77,Edge78,Edge79,Edge80,Edge81,Edge82,Edge83,Edge84,Edge93,+9 more]
FEATURE [Part::Box] Box112  label="Cube100"
  AttacherType = Attacher::AttachEngine3D
  Height = 0.2
  Length = 24
  Placement = pos=(-12,8,3) rot=(0,0,1;0rad)
  Width = 12
FEATURE [Part::MultiFuse] Fusion010006012010005012005027012006002004  label="arm-custom-support-r2"
  Shapes = -> [Box112,Fusion010006012010005012005027012004]
FEATURE [Part::MultiFuse] Fusion010006012010005012005027012006002005  label="arm-exp"
  Shapes = -> [Chamfer030006002016005008003009009003,Fusion010006012010005012005027012006002004]
FEATURE [Part::Chamfer] Chamfer030006002016005008003009009004
  Base = -> Box007
  Edges = 1 edges r=3: [Edge10]
FEATURE [Part::Chamfer] Chamfer030006002016005008003009009005
  Base = -> Box008
  Edges = 1 edges r=3: [Edge10]
FEATURE [Part::Cut] Cut022020016032007036032  label="base-left-mount-btm"
  Base = -> Chamfer030006002016005008003009009004
  Tool = -> Fusion010006012003
FEATURE [Part::Cut] Cut022020016032007036033  label="base-right-arm-btm"
  Base = -> Chamfer030006002016005008003009009005
  Tool = -> Fusion010006012004
FEATURE [Part::Feature] Cut022020016032007036033001  label="base-right-arm-btm001"
  shape: bbox 7.5 x 11 x 14 mm, 16 faces (baked)
FEATURE [Part::Feature] Cut022020016032007036032001  label="base-left-mount-btm001"
  shape: bbox 7.5 x 11 x 14 mm, 16 faces (baked)
FEATURE [Part::MultiFuse] Fusion010006012010005012005027012006002006  label="base-basic"
  Shapes = -> [Cut022020016032007036033,Cut022020016032007036032,Cut022020016006,Cut022020016019,Cut022020016032007036020]
FEATURE [Part::Chamfer] Chamfer030006002016005008003009009006
  Base = -> Cut022020016032007036032001
  Edges = 6 edges r=0.4: [Edge1,Edge2,Edge4,Edge9,Edge13,Edge17]
FEATURE [Part::Chamfer] Chamfer030006002016005008003009009007
  Base = -> Cut022020016032007036033001
  Edges = 6 edges r=0.4: [Edge1,Edge2,Edge4,Edge9,Edge13,Edge17]
FEATURE [Part::MultiFuse] Fusion010006012010005012005027012006002007  label="base-T-slot"
  Shapes = -> [Fusion010006012010005012005027012006002,Chamfer030006002016005008003009009006,Chamfer030006002016005008003009009007]
FEATURE [Part::Feature] Fusion010006012010005012005027012006002007001  label="base-T-slot001"
  shape: bbox 64 x 40 x 24 mm, 155 faces (baked)
FEATURE [Part::MultiFuse] Fusion010006012010005012005027012006002007002  label="base-exp"
  Shapes = -> [Fusion010006012010005012005027012006002007001,Fusion010006012010005012004]
